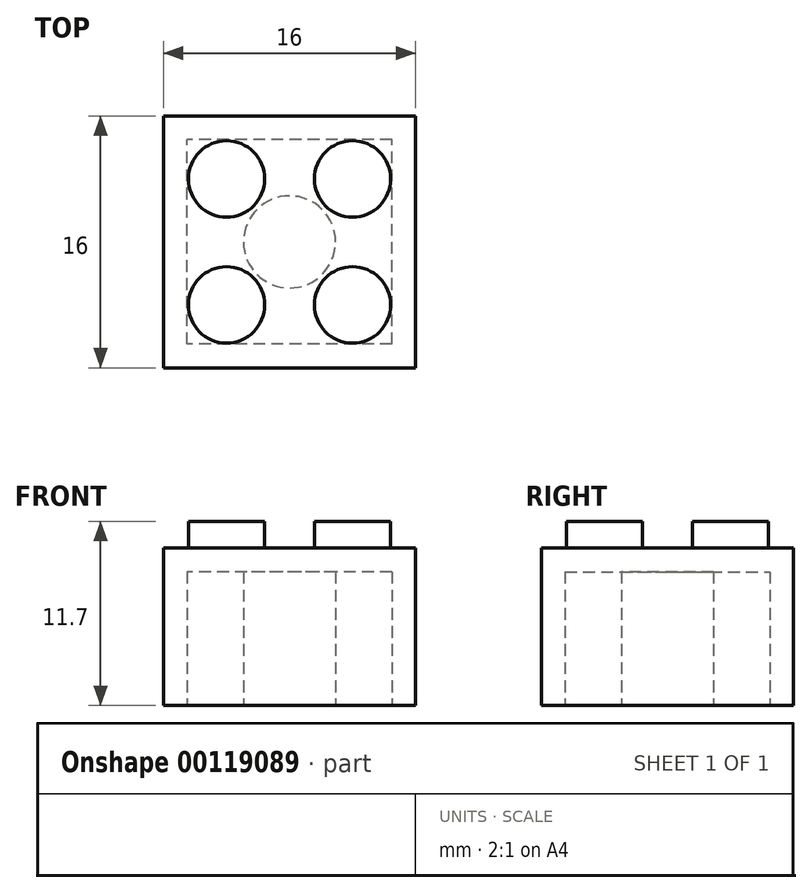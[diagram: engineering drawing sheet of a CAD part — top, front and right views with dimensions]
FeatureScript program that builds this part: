
annotation { "Feature Type Name" : "Feature", "Feature Type Description" : "" }
export const myFeature = defineFeature(function(context is Context, id is Id, definition is map)
    precondition{}
    {
        {
            var Q0;
            Q0=qCreatedBy(makeId("Top.planeOp"),FACE);
            var sketch = newSketch(context, id + "F0", { "sketchPlane" : qUnion([Q0])});
            skLineSegment(sketch, "E0.bottom", {"start": v(8, -8) * mm, "end": v(-8, -8) * mm});
            skLineSegment(sketch, "E0.top", {"start": v(8, 8) * mm, "end": v(-8, 8) * mm});
            skLineSegment(sketch, "E0.left", {"start": v(8, -8) * mm, "end": v(8, 8) * mm});
            skLineSegment(sketch, "E0.right", {"start": v(-8, -8) * mm, "end": v(-8, 8) * mm});
            skPoint(sketch, "E0.middle", {"position": v(0, 0) * mm});
            skSolve(sketch);
        }
        {
            var Q0;
            Q0 = qSketchRegion(id + "F0", true);
            extrude(context, id + "F1", {"entities" : qUnion([Q0]), "depth" : 10 * mm});
        }
        {
            var Q0;
            Q0=makeQuery(id+"F1.opExtrude","CAP_FACE",FACE,{"disambiguationData":[OSD([sQuery(id+"F0.wireOp",EDGE,"E0.bottom"),sQuery(id+"F0.wireOp",EDGE,"E0.top"),sQuery(id+"F0.wireOp",EDGE,"E0.left"),sQuery(id+"F0.wireOp",EDGE,"E0.right")])],"isStart":true});
            shell(context, id + "F2", {"entities" : qUnion([Q0]), "thickness" : 1.5 * mm});
        }
        {
            var Q0;
            Q0=makeQuery(id+"F1.opExtrude","CAP_FACE",FACE,{"disambiguationData":[OSD([sQuery(id+"F0.wireOp",EDGE,"E0.bottom"),sQuery(id+"F0.wireOp",EDGE,"E0.top"),sQuery(id+"F0.wireOp",EDGE,"E0.left"),sQuery(id+"F0.wireOp",EDGE,"E0.right")])],"isStart":false});
            var sketch = newSketch(context, id + "F3", { "sketchPlane" : qUnion([Q0])});
            skCircle(sketch, "E1", {"center": v(-4, -4) * mm, "radius": 2.43 * mm});
            skCircle(sketch, "E2.0.1.0", {"center": v(-4, 4) * mm, "radius": 2.43 * mm});
            skCircle(sketch, "E2.1.0.0", {"center": v(4, -4) * mm, "radius": 2.43 * mm});
            skCircle(sketch, "E2.1.1.0", {"center": v(4, 4) * mm, "radius": 2.43 * mm});
            skLineSegment(sketch, "E2.direction1", {"start": v(-4, -4) * mm, "end": v(4, -4) * mm, "construction": true});
            skLineSegment(sketch, "E2.direction2", {"start": v(-4, -4) * mm, "end": v(-4, 4) * mm, "construction": true});
            skSolve(sketch);
        }
        {
            var Q0;
            Q0 = qSketchRegion(id + "F3", true);
            extrude(context, id + "F4", {"entities" : qUnion([Q0]), "operationType" : NewBodyOperationType.ADD, "depth" : 1.7 * mm});
        }
        {
            var Q0;
            Q0=qCreatedBy(makeId("Top.planeOp"),FACE);
            var sketch = newSketch(context, id + "F5", { "sketchPlane" : qUnion([Q0])});
            skCircle(sketch, "E3", {"center": v(0, 0) * mm, "radius": 2.93 * mm});
            skSolve(sketch);
        }
        {
            var Q0;
            Q0 = qSketchRegion(id + "F5", true);
            extrude(context, id + "F6", {"entities" : qUnion([Q0]), "operationType" : NewBodyOperationType.ADD, "depth" : 10 * mm});
        }
    });
